# Revit family: dBA - 2 inch - Ceiling and Wall Panels 24x24
name_source: partatom
category: Specialty Equipment
units: mm (PartAtom-declared; Revit-internal decimal feet)

## family parameters
Always vertical = No
Cut with Voids When Loaded = No
Enable Cutting in Views = Yes
Maintain Annotation Orientation = No
OmniClass Number = 23.35.00.00
OmniClass Title = Covering, Cladding, and Finishes
Part Type = Normal
Room Calculation Point = No
Round Connector Dimension = Use Diameter
Shared = No
Work Plane-Based = Yes

## types (2) — shared parameters
Acoustics - NRC = Sound absorption varies from NRC 0.45 to 0.95 based on installation method used when tested per ASTM C423.
Assembly Code = C30
Default Elevation = 4' - 0"
Description = dBA Ceiling and Wall Panels
Fire Rating = ASTM E84 - Class A
Manufacturer = Acoustical Surfaces, Inc.
Material = Sound Silencer dBA
Model = Sound Silencer - dBA Ceiling and Wall Panels
Recycled Content Percentage = 0%
Type Comments = dBA Ceiling and Wall Panels
URL = https://www.acousticalsurfaces.com

## per-type parameters (varying)
| type | Finish |
| Charcoal | Paint - Acoustical-Surfaces - dBA - Charcoal |
| White | Paint - Acoustical-Surfaces - dBA - White |

## geometry (parser evidence)
native form markers: Sweep x3
no freeform markers — native parametric forms only
